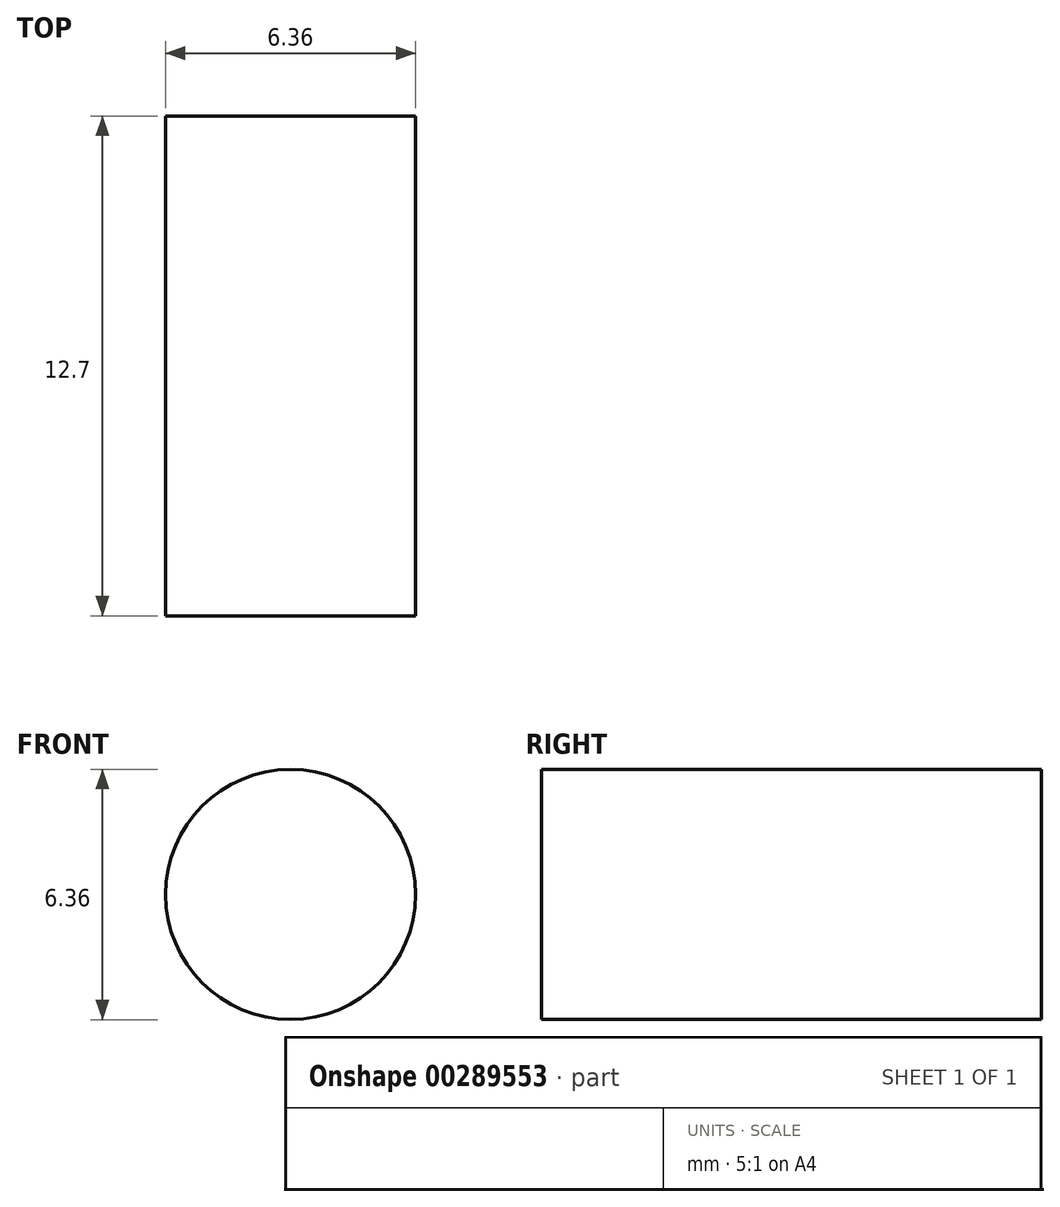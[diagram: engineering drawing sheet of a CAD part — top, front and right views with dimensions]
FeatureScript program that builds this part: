
annotation { "Feature Type Name" : "Feature", "Feature Type Description" : "" }
export const myFeature = defineFeature(function(context is Context, id is Id, definition is map)
    precondition{}
    {
        {
            var Q0;
            Q0=qCreatedBy(makeId("Front.planeOp"),FACE);
            var sketch = newSketch(context, id + "F0", { "sketchPlane" : qUnion([Q0])});
            skCircle(sketch, "E0", {"center": v(0, 0) * mm, "radius": 3.17 * mm});
            skSolve(sketch);
        }
        {
            var Q0;
            Q0=makeQuery(id+"F0.imprint","IMPRINT",FACE,{"disambiguationData":[TD([[makeQuery(id+"F0.imprint","IMPRINT",EDGE,{"derivedFrom":sQuery(id+"F0.wireOp",EDGE,"E0")}),1.0]])]});
            extrude(context, id + "F1", {"entities" : qUnion([Q0]), "depth" : 12.7 * mm});
        }
    });
